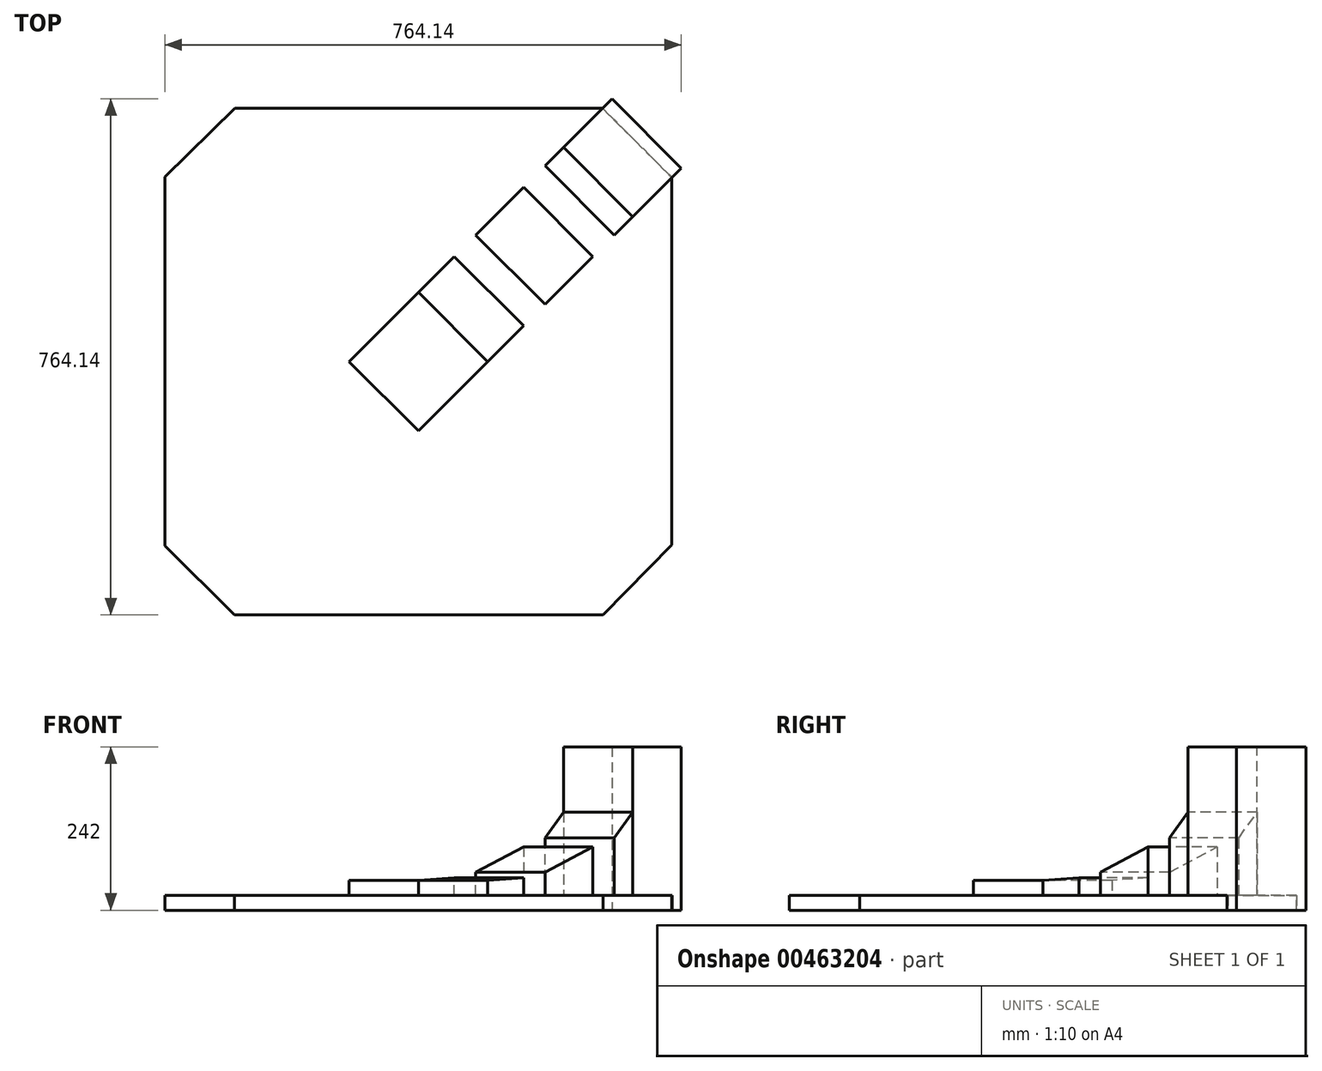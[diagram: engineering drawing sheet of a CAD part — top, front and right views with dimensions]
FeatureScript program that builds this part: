
annotation { "Feature Type Name" : "Feature", "Feature Type Description" : "" }
export const myFeature = defineFeature(function(context is Context, id is Id, definition is map)
    precondition{}
    {
        {
            var Q0;
            Q0=qCreatedBy(makeId("Top.planeOp"),FACE);
            var sketch = newSketch(context, id + "F0", { "sketchPlane" : qUnion([Q0])});
            skLineSegment(sketch, "E0", {"start": v(0, 375) * mm, "end": v(0, -375) * mm, "construction": true});
            skLineSegment(sketch, "E1", {"start": v(-375, 0) * mm, "end": v(375, 0) * mm, "construction": true});
            skLineSegment(sketch, "E2.bottom", {"start": v(-375, 375) * mm, "end": v(375, 375) * mm});
            skLineSegment(sketch, "E2.top", {"start": v(-375, -375) * mm, "end": v(375, -375) * mm});
            skLineSegment(sketch, "E2.left", {"start": v(-375, 375) * mm, "end": v(-375, -375) * mm});
            skLineSegment(sketch, "E2.right", {"start": v(375, 375) * mm, "end": v(375, -375) * mm});
            skLineSegment(sketch, "E3", {"start": v(-375, 273.57) * mm, "end": v(-271.38, 375) * mm});
            skLineSegment(sketch, "E4", {"start": v(-375, -375) * mm, "end": v(375, 375) * mm, "construction": true});
            skLineSegment(sketch, "E5", {"start": v(-375, 375) * mm, "end": v(375, -375) * mm, "construction": true});
            skLineSegment(sketch, "E6", {"start": v(273.57, -375) * mm, "end": v(375, -271.38) * mm});
            skLineSegment(sketch, "E7", {"start": v(272.47, 375) * mm, "end": v(375, 272.47) * mm});
            skLineSegment(sketch, "E8", {"start": v(-375, -272.47) * mm, "end": v(-272.47, -375) * mm});
            skSolve(sketch);
        }
        {
            var Q0;
            {var subQ3=sQuery(id+"F0.wireOp",EDGE,"E3");Q0=makeQuery(id+"F0.imprint","IMPRINT",FACE,{"disambiguationData":[TD([[makeQuery(id+"F0.imprint","IMPRINT",EDGE,{"derivedFrom":subQ3}),-1.0]])]});}
            extrude(context, id + "F1", {"entities" : qUnion([Q0]), "depth" : 22 * mm});
        }
        {
            var Q0;
            Q0=makeQuery(id+"F1.opExtrude","CAP_FACE",FACE,{"disambiguationData":[OSD([sQuery(id+"F0.wireOp",EDGE,"E2.bottom"),sQuery(id+"F0.wireOp",EDGE,"E2.top"),sQuery(id+"F0.wireOp",EDGE,"E2.left"),sQuery(id+"F0.wireOp",EDGE,"E2.right"),sQuery(id+"F0.wireOp",EDGE,"E3"),sQuery(id+"F0.wireOp",EDGE,"E6"),sQuery(id+"F0.wireOp",EDGE,"E7"),sQuery(id+"F0.wireOp",EDGE,"E8")])],"isStart":false});
            var sketch = newSketch(context, id + "F2", { "sketchPlane" : qUnion([Q0])});
            skLineSegment(sketch, "E9", {"start": v(-375, -272.47) * mm, "end": v(272.47, 375) * mm, "construction": true});
            skLineSegment(sketch, "E10", {"start": v(-272.47, -375) * mm, "end": v(375, 272.47) * mm, "construction": true});
            skLineSegment(sketch, "E11", {"start": v(0, 102.53) * mm, "end": v(102.53, 0) * mm});
            skLineSegment(sketch, "E12", {"start": v(-102.53, 0) * mm, "end": v(0, -102.53) * mm});
            skLineSegment(sketch, "E13", {"start": v(-102.53, 0) * mm, "end": v(0, 102.53) * mm});
            skLineSegment(sketch, "E14", {"start": v(0, -102.53) * mm, "end": v(102.53, 0) * mm});
            skLineSegment(sketch, "E15", {"start": v(53.03, 155.56) * mm, "end": v(155.56, 53.03) * mm, "construction": true});
            skSolve(sketch);
        }
        {
            var Q0;
            Q0=makeQuery(id+"F2.imprint","IMPRINT",FACE,{"disambiguationData":[TD([[makeQuery(id+"F2.imprint","IMPRINT",EDGE,{"derivedFrom":sQuery(id+"F2.wireOp",EDGE,"E11")}),-1.0]])]});
            extrude(context, id + "F3", {"entities" : qUnion([Q0]), "operationType" : NewBodyOperationType.ADD, "depth" : 22 * mm});
        }
        {
            var Q0;
            Q0=makeQuery(id+"F3.opExtrude","SWEPT_FACE",FACE,{"disambiguationData":[OSD([sQuery(id+"F2.wireOp",EDGE,"E14")])]});
            var sketch = newSketch(context, id + "F4", { "sketchPlane" : qUnion([Q0])});
            skLineSegment(sketch, "E16", {"start": v(72.5, 22) * mm, "end": v(147.5, 22) * mm});
            skLineSegment(sketch, "E17", {"start": v(147.5, 22) * mm, "end": v(147.5, 48) * mm});
            skLineSegment(sketch, "E18", {"start": v(147.5, 48) * mm, "end": v(72.5, 44) * mm});
            skLineSegment(sketch, "E19", {"start": v(72.5, 44) * mm, "end": v(72.5, 22) * mm});
            skLineSegment(sketch, "E20.0", {"start": v(-72.5, 44) * mm, "end": v(72.5, 44) * mm, "construction": true});
            skLineSegment(sketch, "E21", {"start": v(0, 44) * mm, "end": v(0, 115.84) * mm, "construction": true});
            skPoint(sketch, "E21.endSnap0", {"position": v(0, 44) * mm});
            skLineSegment(sketch, "E22.0", {"start": v(457.83, 22) * mm, "end": v(73.27, 22) * mm, "construction": true});
            skLineSegment(sketch, "E23", {"start": v(192.5, 22) * mm, "end": v(192.5, 56.2) * mm});
            skLineSegment(sketch, "E24", {"start": v(192.5, 56.2) * mm, "end": v(292.5, 94) * mm});
            skLineSegment(sketch, "E25", {"start": v(292.5, 94) * mm, "end": v(292.5, 22) * mm});
            skLineSegment(sketch, "E26", {"start": v(292.5, 22) * mm, "end": v(192.5, 22) * mm});
            skLineSegment(sketch, "E27", {"start": v(337.5, 22) * mm, "end": v(337.5, 107.3) * mm});
            skLineSegment(sketch, "E28", {"start": v(337.5, 107.3) * mm, "end": v(376, 145) * mm});
            skLineSegment(sketch, "E29", {"start": v(376, 145) * mm, "end": v(376, 22) * mm});
            skLineSegment(sketch, "E30", {"start": v(376, 22) * mm, "end": v(337.5, 22) * mm});
            skLineSegment(sketch, "E31", {"start": v(376, 145) * mm, "end": v(376, 242) * mm});
            skLineSegment(sketch, "E32", {"start": v(376, 242) * mm, "end": v(457.83, 242) * mm});
            skLineSegment(sketch, "E33", {"start": v(457.83, 242) * mm, "end": v(457.83, 22) * mm});
            skLineSegment(sketch, "E34", {"start": v(457.83, 22) * mm, "end": v(376, 22) * mm});
            skSolve(sketch);
        }
        {
            var Q0;
            Q0=makeQuery(id+"F4.imprint","IMPRINT",FACE,{"disambiguationData":[TD([[makeQuery(id+"F4.imprint","IMPRINT",EDGE,{"derivedFrom":sQuery(id+"F4.wireOp",EDGE,"E16")}),1.0]])]});
            extrude(context, id + "F5", {"entities" : qUnion([Q0]), "oppositeDirection" : true, "depth" : 145 * mm});
        }
        {
            var Q0;
            Q0=makeQuery(id+"F4.imprint","IMPRINT",FACE,{"disambiguationData":[TD([[makeQuery(id+"F4.imprint","IMPRINT",EDGE,{"derivedFrom":sQuery(id+"F4.wireOp",EDGE,"E23")}),-1.0]])]});
            extrude(context, id + "F6", {"entities" : qUnion([Q0]), "oppositeDirection" : true, "depth" : 145 * mm});
        }
        {
            var Q0;
            Q0=makeQuery(id+"F4.imprint","IMPRINT",FACE,{"disambiguationData":[TD([[makeQuery(id+"F4.imprint","IMPRINT",EDGE,{"derivedFrom":sQuery(id+"F4.wireOp",EDGE,"E27")}),-1.0]])]});
            extrude(context, id + "F7", {"entities" : qUnion([Q0]), "oppositeDirection" : true, "depth" : 145 * mm});
        }
        {
            var Q0;
            Q0=makeQuery(id+"F4.imprint","IMPRINT",FACE,{"disambiguationData":[TD([[makeQuery(id+"F4.imprint","IMPRINT",EDGE,{"derivedFrom":sQuery(id+"F4.wireOp",EDGE,"E29")}),1.0]])]});
            extrude(context, id + "F8", {"entities" : qUnion([Q0]), "oppositeDirection" : true, "depth" : 145 * mm});
        }
        {
            var Q0;
            Q0=makeQuery(id+"F8.opExtrude","SWEPT_FACE",FACE,{"disambiguationData":[OSD([sQuery(id+"F4.wireOp",EDGE,"E33")])]});
            extrude(context, id + "F9", {"entities" : qUnion([Q0]), "operationType" : NewBodyOperationType.ADD, "depth" : 20 * mm});
        }
        {
            var Q0;
            {var subQ0=sQuery(id+"F4.wireOp",EDGE,"E34");Q0=makeQuery(id+"F9.boolean.opBoolean","MERGE",FACE,{"derivedFrom":[makeQuery(id+"F8.opExtrude","SWEPT_FACE",FACE,{"disambiguationData":[OSD([subQ0])]}),makeQuery(id+"F9.opExtrude","SWEPT_FACE",FACE,{"disambiguationData":[OSD([sQuery(id+"F4.wireOp",EDGE,"E33"),subQ0])]})]});}
            var sketch = newSketch(context, id + "F10", { "sketchPlane" : qUnion([Q0])});
            skLineSegment(sketch, "E35.0", {"start": v(286.61, -389.14) * mm, "end": v(389.14, -286.61) * mm});
            skLineSegment(sketch, "E36", {"start": v(389.14, -286.61) * mm, "end": v(375.25, -272.72) * mm});
            skLineSegment(sketch, "E37", {"start": v(375.25, -272.72) * mm, "end": v(272.72, -375.25) * mm});
            skLineSegment(sketch, "E38", {"start": v(272.72, -375.25) * mm, "end": v(286.61, -389.14) * mm});
            skSolve(sketch);
        }
        {
            var Q0;
            Q0=makeQuery(id+"F10.imprint","IMPRINT",FACE,{"disambiguationData":[TD([[makeQuery(id+"F10.imprint","IMPRINT",EDGE,{"derivedFrom":sQuery(id+"F10.wireOp",EDGE,"E35.0")}),1.0]])]});
            extrude(context, id + "F11", {"entities" : qUnion([Q0]), "operationType" : NewBodyOperationType.ADD, "depth" : 22 * mm});
        }
    });
